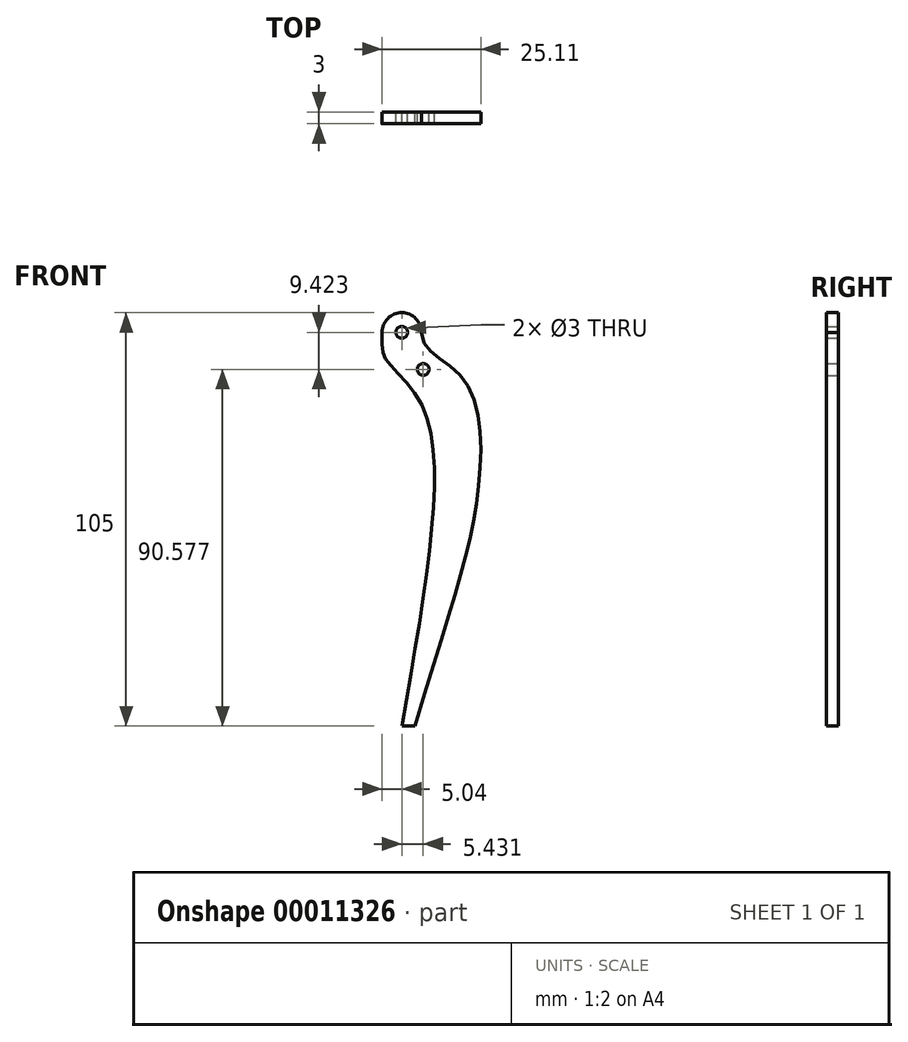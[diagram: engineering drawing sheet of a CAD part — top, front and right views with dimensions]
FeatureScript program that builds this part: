
annotation { "Feature Type Name" : "Feature", "Feature Type Description" : "" }
export const myFeature = defineFeature(function(context is Context, id is Id, definition is map)
    precondition{}
    {
        {
            var Q0;
            Q0=qCreatedBy(makeId("Front.planeOp"),FACE);
            var sketch = newSketch(context, id + "F0", { "sketchPlane" : qUnion([Q0])});
            skCircle(sketch, "E0", {"center": v(0, 0) * mm, "radius": 1.5 * mm});
            skArc(sketch, "E1", {"start": v(5, 0) * mm, "mid": v(0, 5) * mm, "end": v(-5, 0) * mm});
            skFitSpline(sketch, "E2", {"points": [v(5, 0) * mm, v(15.39, -11.47) * mm, v(19.15, -42.05) * mm, v(3.32, -100) * mm], "startDerivative": vector(-2.03, -69.82) * mm, "endDerivative": vector(-59.3, -197.82) * mm});
            skLineSegment(sketch, "E3", {"start": v(0, -100) * mm, "end": v(3.32, -100) * mm});
            skFitSpline(sketch, "E4", {"points": [v(-5, 0) * mm, v(-3.85, -7.12) * mm, v(4.47, -17.35) * mm, v(8.06, -43.92) * mm, v(0, -100) * mm], "startDerivative": vector(-1.93, -84.73) * mm, "endDerivative": vector(-26.45, -151.77) * mm});
            skCircle(sketch, "E5", {"center": v(5.43, -9.42) * mm, "radius": 1.5 * mm});
            skSolve(sketch);
        }
        {
            var Q0;
            Q0 = qSketchRegion(id + "F0", true);
            extrude(context, id + "F1", {"entities" : qUnion([Q0]), "depth" : 3 * mm});
        }
    });
